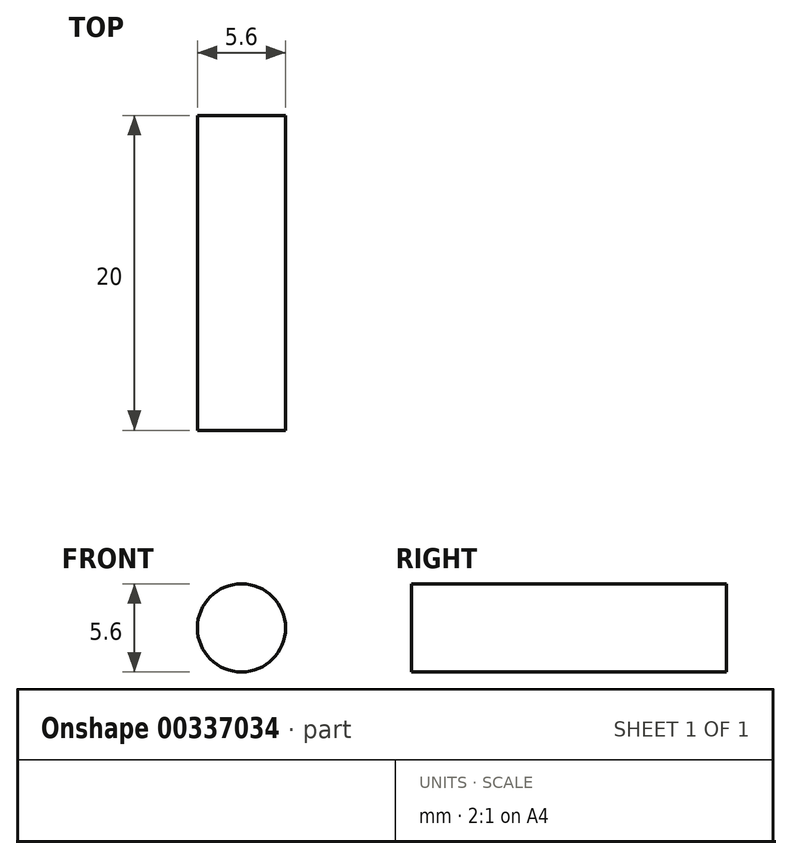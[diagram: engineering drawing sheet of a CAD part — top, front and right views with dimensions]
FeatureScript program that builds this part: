
annotation { "Feature Type Name" : "Feature", "Feature Type Description" : "" }
export const myFeature = defineFeature(function(context is Context, id is Id, definition is map)
    precondition{}
    {
        {
            var Q0;
            Q0=qCreatedBy(makeId("Front.planeOp"),FACE);
            var sketch = newSketch(context, id + "F0", { "sketchPlane" : qUnion([Q0])});
            skCircle(sketch, "E0", {"center": v(0, 0) * mm, "radius": 2.8 * mm});
            skSolve(sketch);
        }
        {
            var Q0;
            Q0=makeQuery(id+"F0.imprint","IMPRINT",FACE,{"disambiguationData":[TD([[makeQuery(id+"F0.imprint","IMPRINT",EDGE,{"derivedFrom":sQuery(id+"F0.wireOp",EDGE,"E0")}),1.0]])]});
            extrude(context, id + "F1", {"entities" : qUnion([Q0]), "depth" : 20 * mm});
        }
    });
